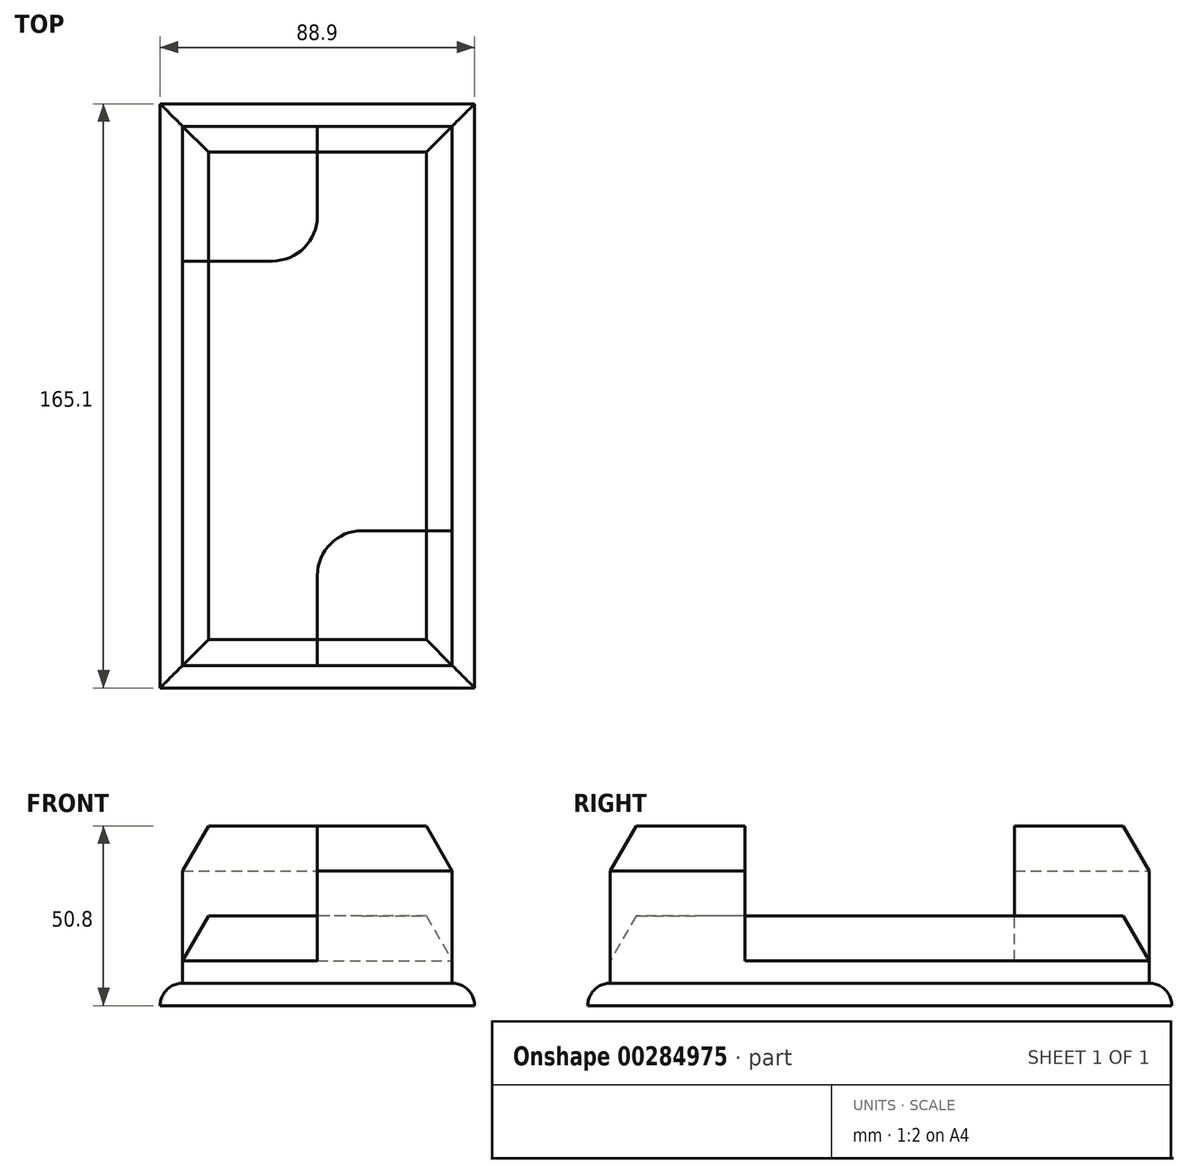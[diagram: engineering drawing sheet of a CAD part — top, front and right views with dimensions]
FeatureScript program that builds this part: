
annotation { "Feature Type Name" : "Feature", "Feature Type Description" : "" }
export const myFeature = defineFeature(function(context is Context, id is Id, definition is map)
    precondition{}
    {
        {
            var Q0;
            Q0=qCreatedBy(makeId("Top.planeOp"),FACE);
            var sketch = newSketch(context, id + "F0", { "sketchPlane" : qUnion([Q0])});
            skLineSegment(sketch, "E0.bottom", {"start": v(-44.45, 82.55) * mm, "end": v(44.45, 82.55) * mm});
            skLineSegment(sketch, "E0.top", {"start": v(-44.45, -82.55) * mm, "end": v(44.45, -82.55) * mm});
            skLineSegment(sketch, "E0.left", {"start": v(-44.45, 82.55) * mm, "end": v(-44.45, -82.55) * mm});
            skLineSegment(sketch, "E0.right", {"start": v(44.45, 82.55) * mm, "end": v(44.45, -82.55) * mm});
            skPoint(sketch, "E0.middle", {"position": v(0, 0) * mm});
            skLineSegment(sketch, "E1.bottom", {"start": v(-38.1, 76.2) * mm, "end": v(38.1, 76.2) * mm});
            skLineSegment(sketch, "E1.top", {"start": v(-38.1, -76.2) * mm, "end": v(38.1, -76.2) * mm});
            skLineSegment(sketch, "E1.left", {"start": v(-38.1, 76.2) * mm, "end": v(-38.1, -76.2) * mm});
            skLineSegment(sketch, "E1.right", {"start": v(38.1, 76.2) * mm, "end": v(38.1, -76.2) * mm});
            skPoint(sketch, "E2", {"position": v(0, 76.2) * mm});
            skLineSegment(sketch, "E3", {"start": v(0, 76.2) * mm, "end": v(0, 50.8) * mm});
            skLineSegment(sketch, "E4", {"start": v(-12.7, 38.1) * mm, "end": v(-38.1, 38.1) * mm});
            skPoint(sketch, "E5", {"position": v(0, -76.2) * mm});
            skLineSegment(sketch, "E6", {"start": v(0, -76.2) * mm, "end": v(0, -50.8) * mm});
            skLineSegment(sketch, "E7", {"start": v(12.7, -38.1) * mm, "end": v(38.1, -38.1) * mm});
            skPoint(sketch, "E8.visualSharp", {"position": v(0, 38.1) * mm});
            skArc(sketch, "E8.filletArc", {"start": v(-12.7, 38.1) * mm, "mid": v(-3.72, 41.82) * mm, "end": v(0, 50.8) * mm});
            skPoint(sketch, "E9.visualSharp", {"position": v(0, -38.1) * mm});
            skArc(sketch, "E9.filletArc", {"start": v(12.7, -38.1) * mm, "mid": v(3.72, -41.82) * mm, "end": v(0, -50.8) * mm});
            skSolve(sketch);
        }
        {
            var Q0;
            Q0=makeQuery(id+"F0.imprint","IMPRINT",FACE,{"disambiguationData":[TD([[makeQuery(id+"F0.imprint","IMPRINT",EDGE,{"derivedFrom":sQuery(id+"F0.wireOp",EDGE,"E0.bottom")}),-1.0]])]});
            extrude(context, id + "F1", {"entities" : qUnion([Q0]), "depth" : 6.35 * mm});
        }
        {
            var Q0;
            {var subQ9=sQuery(id+"F0.wireOp",EDGE,"E3");Q0=makeQuery(id+"F0.imprint","IMPRINT",FACE,{"disambiguationData":[TD([[makeQuery(id+"F0.imprint","IMPRINT",EDGE,{"derivedFrom":subQ9}),1.0]])]});}
            extrude(context, id + "F2", {"entities" : qUnion([Q0]), "operationType" : NewBodyOperationType.ADD, "depth" : 25.4 * mm});
        }
        {
            var Q0;
            {var subQ1=sQuery(id+"F0.wireOp",EDGE,"E6");Q0=makeQuery(id+"F0.imprint","IMPRINT",FACE,{"disambiguationData":[TD([[makeQuery(id+"F0.imprint","IMPRINT",EDGE,{"derivedFrom":subQ1}),-1.0]])]});}
            var Q1;
            {var subQ0=sQuery(id+"F0.wireOp",EDGE,"E3");Q1=makeQuery(id+"F0.imprint","IMPRINT",FACE,{"disambiguationData":[TD([[makeQuery(id+"F0.imprint","IMPRINT",EDGE,{"derivedFrom":subQ0}),-1.0]])]});}
            extrude(context, id + "F3", {"entities" : qUnion([Q0, Q1]), "operationType" : NewBodyOperationType.ADD, "depth" : 50.8 * mm});
        }
        {
            var Q0;
            Q0=makeQuery(id+"F3.opExtrude","CAP_EDGE",EDGE,{"disambiguationData":[OSD([sQuery(id+"F0.wireOp",EDGE,"E1.top")])],"isStart":false});
            var Q1;
            Q1=makeQuery(id+"F3.opExtrude","CAP_EDGE",EDGE,{"disambiguationData":[OSD([sQuery(id+"F0.wireOp",EDGE,"E1.right")])],"isStart":false});
            chamfer(context, id + "F4", {"entities" : qUnion([Q0, Q1]), "chamferType" : ChamferType.OFFSET_ANGLE, "width" : 12.7 * mm, "oppositeDirection" : true, "angle" : 30 * degree, "tangentPropagation" : true});
        }
        {
            var Q0;
            Q0=makeQuery(id+"F1.opExtrude","CAP_EDGE",EDGE,{"disambiguationData":[OSD([sQuery(id+"F0.wireOp",EDGE,"E0.top")])],"isStart":false});
            var Q1;
            Q1=makeQuery(id+"F1.opExtrude","CAP_EDGE",EDGE,{"disambiguationData":[OSD([sQuery(id+"F0.wireOp",EDGE,"E0.right")])],"isStart":false});
            var Q2;
            Q2=makeQuery(id+"F1.opExtrude","CAP_EDGE",EDGE,{"disambiguationData":[OSD([sQuery(id+"F0.wireOp",EDGE,"E0.bottom")])],"isStart":false});
            var Q3;
            Q3=makeQuery(id+"F1.opExtrude","CAP_EDGE",EDGE,{"disambiguationData":[OSD([sQuery(id+"F0.wireOp",EDGE,"E0.left")])],"isStart":false});
            fillet(context, id + "F5", {"entities" : qUnion([Q0, Q1, Q2, Q3]), "radius" : 6.35 * mm, "tangentPropagation" : true, "allowEdgeOverflow" : false});
        }
        {
            var Q0;
            Q0=makeQuery(id+"F3.opExtrude","CAP_EDGE",EDGE,{"disambiguationData":[OSD([sQuery(id+"F0.wireOp",EDGE,"E1.bottom")])],"isStart":false});
            var Q1;
            Q1=makeQuery(id+"F3.opExtrude","CAP_EDGE",EDGE,{"disambiguationData":[OSD([sQuery(id+"F0.wireOp",EDGE,"E1.left")])],"isStart":false});
            chamfer(context, id + "F6", {"entities" : qUnion([Q0, Q1]), "chamferType" : ChamferType.OFFSET_ANGLE, "width" : 12.7 * mm, "oppositeDirection" : false, "angle" : 30 * degree, "tangentPropagation" : true});
        }
        {
            var Q0;
            Q0=makeQuery(id+"F2.opExtrude","CAP_EDGE",EDGE,{"disambiguationData":[OSD([sQuery(id+"F0.wireOp",EDGE,"E1.right")])],"isStart":false});
            var Q1;
            Q1=makeQuery(id+"F2.opExtrude","CAP_EDGE",EDGE,{"disambiguationData":[OSD([sQuery(id+"F0.wireOp",EDGE,"E1.bottom")])],"isStart":false});
            var Q2;
            Q2=makeQuery(id+"F2.opExtrude","CAP_EDGE",EDGE,{"disambiguationData":[OSD([sQuery(id+"F0.wireOp",EDGE,"E1.left")])],"isStart":false});
            var Q3;
            Q3=makeQuery(id+"F2.opExtrude","CAP_EDGE",EDGE,{"disambiguationData":[OSD([sQuery(id+"F0.wireOp",EDGE,"E1.top")])],"isStart":false});
            chamfer(context, id + "F7", {"entities" : qUnion([Q0, Q1, Q2, Q3]), "chamferType" : ChamferType.OFFSET_ANGLE, "width" : 12.7 * mm, "oppositeDirection" : false, "angle" : 30 * degree, "tangentPropagation" : true});
        }
    });
